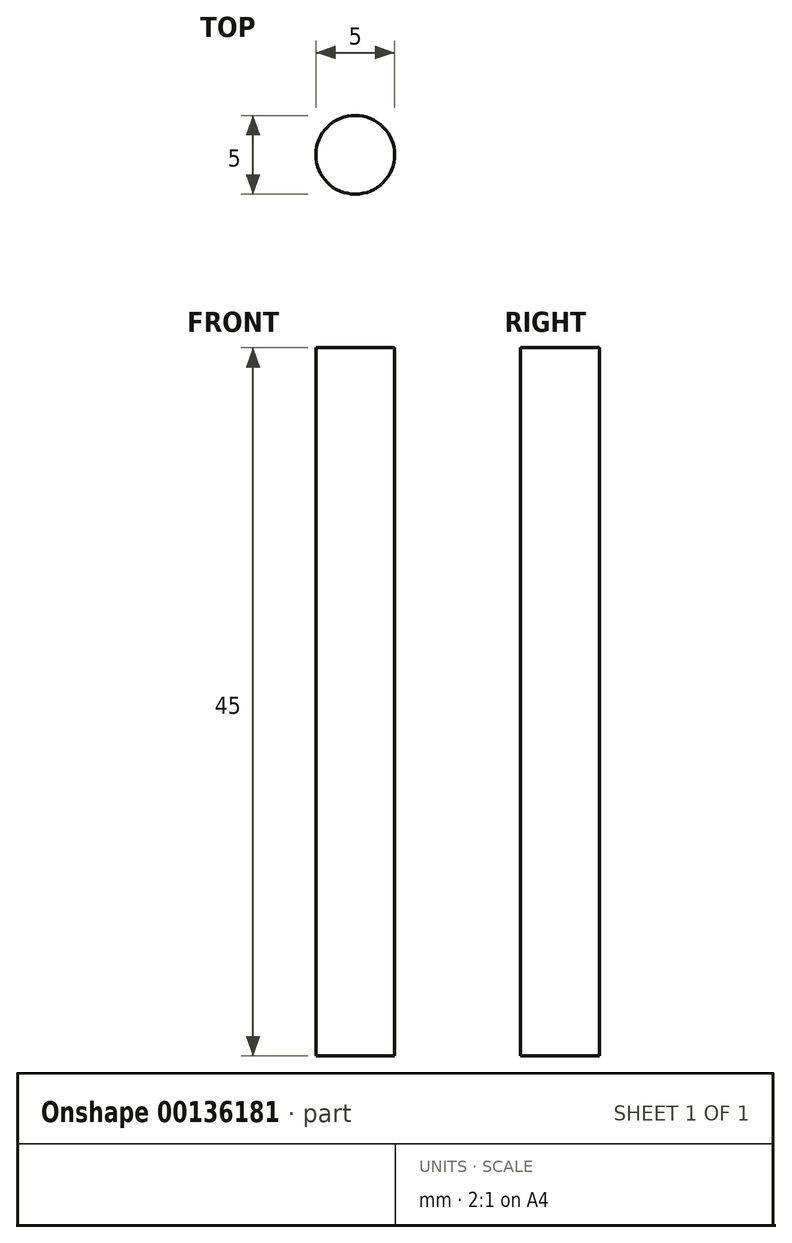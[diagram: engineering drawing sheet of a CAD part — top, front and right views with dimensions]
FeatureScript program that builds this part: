
annotation { "Feature Type Name" : "Feature", "Feature Type Description" : "" }
export const myFeature = defineFeature(function(context is Context, id is Id, definition is map)
    precondition{}
    {
        {
            var Q0;
            Q0=qCreatedBy(makeId("Top.planeOp"),FACE);
            var sketch = newSketch(context, id + "F0", { "sketchPlane" : qUnion([Q0])});
            skCircle(sketch, "E0", {"center": v(0, 0) * mm, "radius": 2.5 * mm});
            skSolve(sketch);
        }
        {
            var Q0;
            Q0 = qSketchRegion(id + "F0", true);
            extrude(context, id + "F1", {"entities" : qUnion([Q0]), "depth" : 45 * mm});
        }
    });
